# Revit family: HermanMiller_Seating_Aeron_WorkStool_High
name_source: partatom
category: Furniture
revit_build: Autodesk Revit Architecture 2012 (Build: 20110309_2315(x64)
units: mm (PartAtom-declared; Revit-internal decimal feet)

## types (1)
- Aeron Workstool High
    Arm On = Yes
    Armpad Finish = Herman Miller - Finish BK Black
    Assembly Code = E2020200
    Base Finish = Herman Miller - Finish G1 Graphite
    Catalog = Seating (HST)
    Description = Wk Chr Aeron Std-Ht Pneu Tlt Lim/Ang Ht Adj Arms NonuphstPds/B
    Frame Finish = Herman Miller - Finish G1 Graphite
    Lumbar Finish = Herman Miller - Finish BK Black
    Lumbar Support = No
    Manufacturer = Herman Miller, Inc.
    Model = AE113HWB N2 G1
    PostureFit Finish = Herman Miller - Finish G1 Graphite
    PostureFit support = Yes
    Product Documentation Link = http://www.hermanmiller.com
    Seat Material = Herman Miller - Pellicle 3D01 Classic Carbon
    Type Comments = Aeron Work Chair - AE72 Series
    URL = http://www.hermanmiller.com

## geometry (parser evidence)
native form markers: Blend x20, Sweep x2
no freeform markers — native parametric forms only
